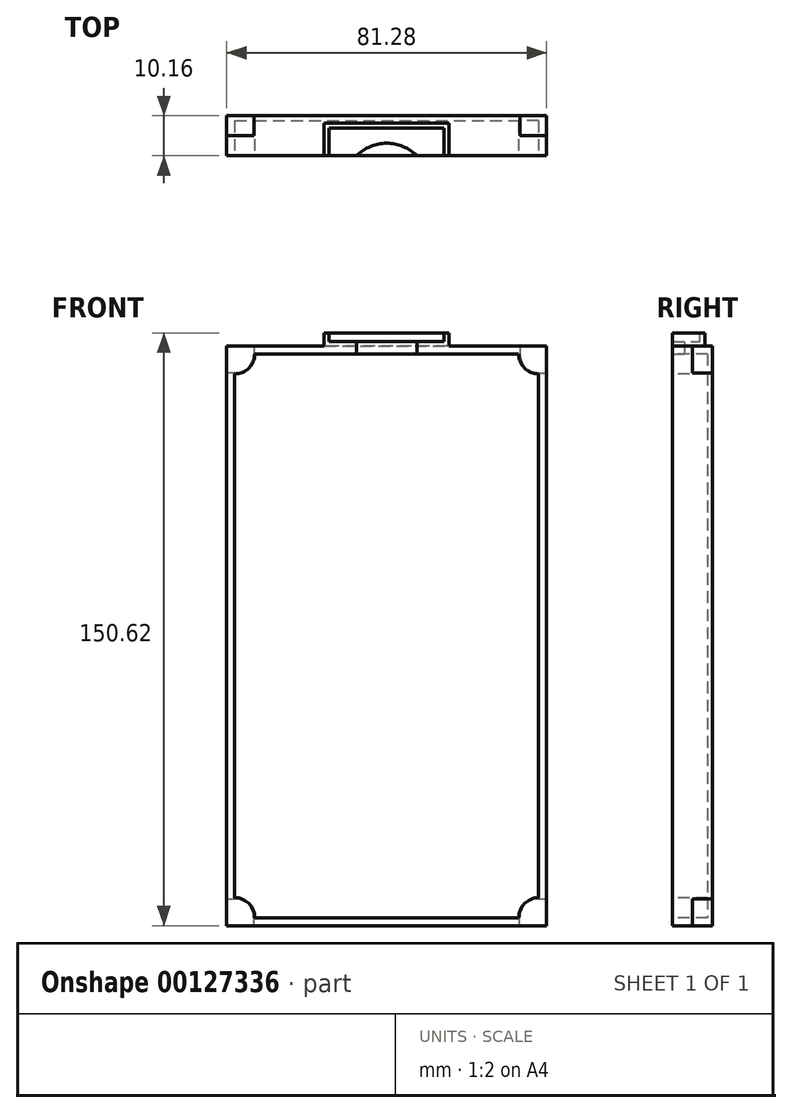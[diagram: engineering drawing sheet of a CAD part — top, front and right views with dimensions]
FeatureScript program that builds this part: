
annotation { "Feature Type Name" : "Feature", "Feature Type Description" : "" }
export const myFeature = defineFeature(function(context is Context, id is Id, definition is map)
    precondition{}
    {
        {
            var Q0;
            Q0=qCreatedBy(makeId("Front.planeOp"),FACE);
            var sketch = newSketch(context, id + "F0", { "sketchPlane" : qUnion([Q0])});
            skLineSegment(sketch, "E0", {"start": v(-47.34, 99.33) * mm, "end": v(-47.34, -48) * mm});
            skLineSegment(sketch, "E1", {"start": v(-47.34, -48) * mm, "end": v(33.94, -48) * mm});
            skLineSegment(sketch, "E2", {"start": v(33.94, -48) * mm, "end": v(33.94, 99.33) * mm});
            skLineSegment(sketch, "E3", {"start": v(33.94, 99.33) * mm, "end": v(-47.34, 99.33) * mm});
            skSolve(sketch);
        }
        {
            var Q0;
            Q0 = qSketchRegion(id + "F0", true);
            extrude(context, id + "F1", {"entities" : qUnion([Q0]), "depth" : 10.16 * mm});
        }
        {
            var Q0;
            Q0=makeQuery(id+"F1.opExtrude","CAP_FACE",FACE,{"disambiguationData":[OSD([sQuery(id+"F0.wireOp",EDGE,"E0"),sQuery(id+"F0.wireOp",EDGE,"E1"),sQuery(id+"F0.wireOp",EDGE,"E2"),sQuery(id+"F0.wireOp",EDGE,"E3")])],"isStart":false});
            var sketch = newSketch(context, id + "F2", { "sketchPlane" : qUnion([Q0])});
            skLineSegment(sketch, "E4", {"start": v(-45.31, 97.3) * mm, "end": v(-45.31, -45.96) * mm});
            skLineSegment(sketch, "E5", {"start": v(-45.31, -45.96) * mm, "end": v(31.9, -45.96) * mm});
            skLineSegment(sketch, "E6", {"start": v(31.9, -45.96) * mm, "end": v(31.9, 97.3) * mm});
            skLineSegment(sketch, "E7", {"start": v(31.9, 97.3) * mm, "end": v(-45.31, 97.3) * mm});
            skSolve(sketch);
        }
        {
            var Q0;
            Q0 = qSketchRegion(id + "F2", true);
            extrude(context, id + "F3", {"entities" : qUnion([Q0]), "operationType" : NewBodyOperationType.REMOVE, "oppositeDirection" : true, "depth" : 8.9 * mm});
        }
        {
            var Q0;
            Q0=makeQuery(id+"F1.opExtrude","CAP_FACE",FACE,{"disambiguationData":[OSD([sQuery(id+"F0.wireOp",EDGE,"E0"),sQuery(id+"F0.wireOp",EDGE,"E1"),sQuery(id+"F0.wireOp",EDGE,"E2"),sQuery(id+"F0.wireOp",EDGE,"E3")])],"isStart":false});
            var sketch = newSketch(context, id + "F4", { "sketchPlane" : qUnion([Q0])});
            skArc(sketch, "E8", {"start": v(-40.23, 97.3) * mm, "mid": v(-41.72, 93.7) * mm, "end": v(-45.31, 92.21) * mm});
            skLineSegment(sketch, "E9", {"start": v(-45.31, 97.3) * mm, "end": v(-45.31, 92.21) * mm});
            skLineSegment(sketch, "E10", {"start": v(-45.31, 97.3) * mm, "end": v(-40.23, 97.3) * mm});
            skArc(sketch, "E11", {"start": v(26.82, 97.3) * mm, "mid": v(28.31, 93.7) * mm, "end": v(31.9, 92.21) * mm});
            skLineSegment(sketch, "E12", {"start": v(31.9, 97.3) * mm, "end": v(26.82, 97.3) * mm});
            skLineSegment(sketch, "E13", {"start": v(31.9, 97.3) * mm, "end": v(31.9, 92.21) * mm});
            skArc(sketch, "E14", {"start": v(-45.31, -40.88) * mm, "mid": v(-41.72, -42.37) * mm, "end": v(-40.23, -45.96) * mm});
            skLineSegment(sketch, "E15", {"start": v(-45.31, -40.88) * mm, "end": v(-45.31, -45.96) * mm});
            skLineSegment(sketch, "E16", {"start": v(-40.23, -45.96) * mm, "end": v(-45.31, -45.96) * mm});
            skArc(sketch, "E17", {"start": v(26.82, -45.96) * mm, "mid": v(28.31, -42.37) * mm, "end": v(31.9, -40.88) * mm});
            skLineSegment(sketch, "E18", {"start": v(31.9, -40.88) * mm, "end": v(31.9, -45.96) * mm});
            skLineSegment(sketch, "E19", {"start": v(26.82, -45.96) * mm, "end": v(31.9, -45.96) * mm});
            skSolve(sketch);
        }
        {
            var Q0;
            Q0 = qSketchRegion(id + "F4", true);
            extrude(context, id + "F5", {"entities" : qUnion([Q0]), "operationType" : NewBodyOperationType.ADD, "oppositeDirection" : true, "depth" : 10.16 * mm});
        }
        {
            var Q0;
            Q0=makeQuery(id+"F1.opExtrude","SWEPT_FACE",FACE,{"disambiguationData":[OSD([sQuery(id+"F0.wireOp",EDGE,"E3")])]});
            var sketch = newSketch(context, id + "F6", { "sketchPlane" : qUnion([Q0])});
            skLineSegment(sketch, "E20", {"start": v(-22.58, -10.16) * mm, "end": v(-22.58, -1.9) * mm});
            skLineSegment(sketch, "E21", {"start": v(-22.58, -1.9) * mm, "end": v(9.17, -1.9) * mm});
            skLineSegment(sketch, "E22", {"start": v(9.17, -1.9) * mm, "end": v(9.17, -10.16) * mm});
            skLineSegment(sketch, "E23", {"start": v(-22.58, -10.16) * mm, "end": v(9.17, -10.16) * mm});
            skSolve(sketch);
        }
        {
            var Q0;
            Q0 = qSketchRegion(id + "F6", true);
            extrude(context, id + "F7", {"entities" : qUnion([Q0]), "operationType" : NewBodyOperationType.ADD, "depth" : 3.3 * mm});
        }
        {
            var Q0;
            Q0=makeQuery(id+"F7.opExtrude","CAP_FACE",FACE,{"disambiguationData":[OSD([sQuery(id+"F6.wireOp",EDGE,"E20"),sQuery(id+"F6.wireOp",EDGE,"E21"),sQuery(id+"F6.wireOp",EDGE,"E22"),sQuery(id+"F6.wireOp",EDGE,"E23")])],"isStart":false});
            var sketch = newSketch(context, id + "F8", { "sketchPlane" : qUnion([Q0])});
            skLineSegment(sketch, "E24", {"start": v(-21.3, -10.16) * mm, "end": v(-21.3, -3.18) * mm});
            skLineSegment(sketch, "E25", {"start": v(-21.3, -3.18) * mm, "end": v(7.9, -3.17) * mm});
            skLineSegment(sketch, "E26", {"start": v(7.9, -3.17) * mm, "end": v(7.9, -10.16) * mm});
            skLineSegment(sketch, "E27", {"start": v(-21.3, -10.16) * mm, "end": v(7.9, -10.16) * mm});
            skSolve(sketch);
        }
        {
            var Q0;
            Q0 = qSketchRegion(id + "F8", true);
            extrude(context, id + "F9", {"entities" : qUnion([Q0]), "operationType" : NewBodyOperationType.REMOVE, "oppositeDirection" : true, "depth" : 2.16 * mm});
        }
        {
            var Q0;
            Q0=makeQuery(id+"F9.boolean.opBoolean","COPY",FACE,{"derivedFrom":makeQuery(id+"F9.opExtrude","CAP_FACE",FACE,{"disambiguationData":[OSD([sQuery(id+"F8.wireOp",EDGE,"E24"),sQuery(id+"F8.wireOp",EDGE,"E25"),sQuery(id+"F8.wireOp",EDGE,"E26"),sQuery(id+"F8.wireOp",EDGE,"E27")])],"isStart":false})});
            var sketch = newSketch(context, id + "F10", { "sketchPlane" : qUnion([Q0])});
            skArc(sketch, "E28", {"start": v(0.94, -10.16) * mm, "mid": v(-6.7, -6.99) * mm, "end": v(-14.35, -10.16) * mm});
            skLineSegment(sketch, "E29", {"start": v(0.94, -10.16) * mm, "end": v(-14.35, -10.16) * mm});
            skSolve(sketch);
        }
        {
            var Q0;
            Q0 = qSketchRegion(id + "F10", true);
            extrude(context, id + "F11", {"entities" : qUnion([Q0]), "operationType" : NewBodyOperationType.REMOVE, "oppositeDirection" : true, "depth" : 25.4 * mm});
        }
        {
            var Q0;
            Q0=makeQuery(id+"F1.opExtrude","CAP_FACE",FACE,{"disambiguationData":[OSD([sQuery(id+"F0.wireOp",EDGE,"E0"),sQuery(id+"F0.wireOp",EDGE,"E1"),sQuery(id+"F0.wireOp",EDGE,"E2"),sQuery(id+"F0.wireOp",EDGE,"E3")])],"isStart":true});
            var sketch = newSketch(context, id + "F12", { "sketchPlane" : qUnion([Q0])});
            skArc(sketch, "E30", {"start": v(-27.14, 97.3) * mm, "mid": v(-28.56, 93.88) * mm, "end": v(-31.97, 92.47) * mm});
            skLineSegment(sketch, "E31", {"start": v(-31.97, 92.47) * mm, "end": v(-33.94, 92.47) * mm});
            skLineSegment(sketch, "E32", {"start": v(-33.94, 92.47) * mm, "end": v(-33.94, 99.33) * mm});
            skLineSegment(sketch, "E33", {"start": v(-33.94, 99.33) * mm, "end": v(-27.14, 99.33) * mm});
            skLineSegment(sketch, "E34", {"start": v(-27.14, 99.33) * mm, "end": v(-27.14, 97.3) * mm});
            skArc(sketch, "E35", {"start": v(40.48, 97.3) * mm, "mid": v(41.9, 93.88) * mm, "end": v(45.3, 92.47) * mm});
            skLineSegment(sketch, "E36", {"start": v(45.3, 92.47) * mm, "end": v(47.34, 92.47) * mm});
            skLineSegment(sketch, "E37", {"start": v(47.34, 92.47) * mm, "end": v(47.34, 99.33) * mm});
            skLineSegment(sketch, "E38", {"start": v(47.34, 99.33) * mm, "end": v(40.48, 99.33) * mm});
            skLineSegment(sketch, "E39", {"start": v(40.48, 99.33) * mm, "end": v(40.48, 97.3) * mm});
            skArc(sketch, "E40", {"start": v(-31.9, -41.14) * mm, "mid": v(-28.5, -42.55) * mm, "end": v(-27.08, -45.96) * mm});
            skLineSegment(sketch, "E41", {"start": v(-31.9, -41.14) * mm, "end": v(-33.94, -41.14) * mm});
            skLineSegment(sketch, "E42", {"start": v(-33.94, -41.14) * mm, "end": v(-33.94, -48) * mm});
            skLineSegment(sketch, "E43", {"start": v(-33.94, -48) * mm, "end": v(-27.08, -48) * mm});
            skLineSegment(sketch, "E44", {"start": v(-27.08, -48) * mm, "end": v(-27.08, -45.96) * mm});
            skArc(sketch, "E45", {"start": v(45.31, -41.2) * mm, "mid": v(41.9, -42.62) * mm, "end": v(40.48, -46.03) * mm});
            skLineSegment(sketch, "E46", {"start": v(40.48, -46.03) * mm, "end": v(40.48, -48) * mm});
            skLineSegment(sketch, "E47", {"start": v(40.48, -48) * mm, "end": v(47.34, -48) * mm});
            skLineSegment(sketch, "E48", {"start": v(47.34, -48) * mm, "end": v(47.34, -41.2) * mm});
            skLineSegment(sketch, "E49", {"start": v(47.34, -41.2) * mm, "end": v(45.31, -41.2) * mm});
            skSolve(sketch);
        }
        {
            var Q0;
            Q0 = qSketchRegion(id + "F12", true);
            extrude(context, id + "F13", {"entities" : qUnion([Q0]), "operationType" : NewBodyOperationType.REMOVE, "oppositeDirection" : true, "depth" : 5.08 * mm});
        }
    });
